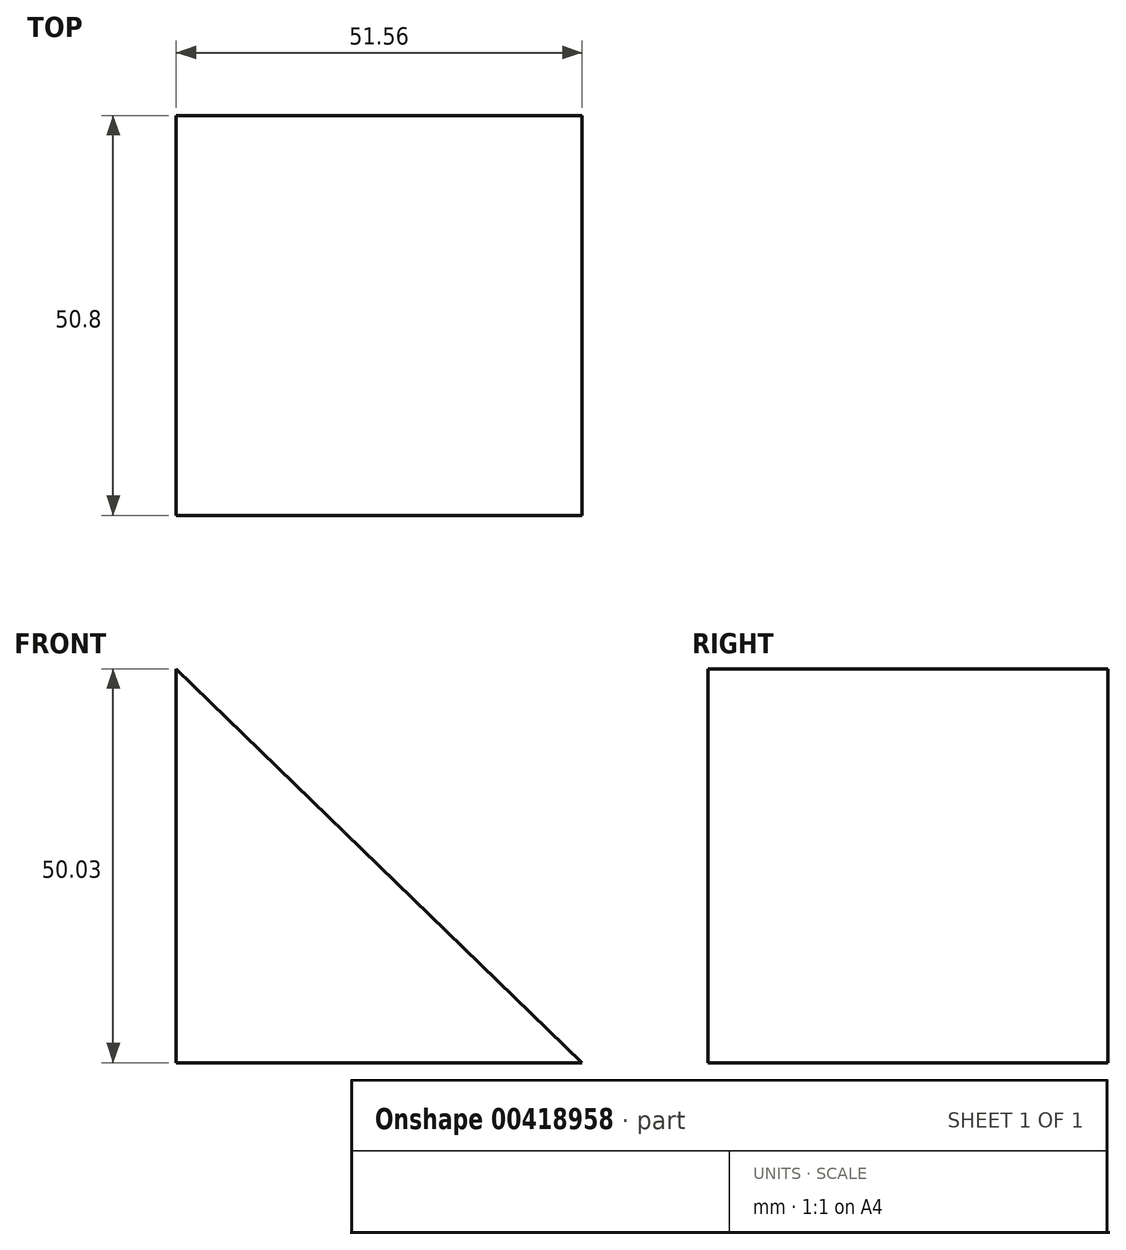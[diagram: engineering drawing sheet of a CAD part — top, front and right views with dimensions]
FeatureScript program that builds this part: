
annotation { "Feature Type Name" : "Feature", "Feature Type Description" : "" }
export const myFeature = defineFeature(function(context is Context, id is Id, definition is map)
    precondition{}
    {
        {
            var Q0;
            Q0=qCreatedBy(makeId("Front.planeOp"),FACE);
            var sketch = newSketch(context, id + "F0", { "sketchPlane" : qUnion([Q0])});
            skLineSegment(sketch, "E0", {"start": v(0, 0) * mm, "end": v(-51.56, 0) * mm});
            skLineSegment(sketch, "E1", {"start": v(-51.56, 50.03) * mm, "end": v(-51.56, 0) * mm});
            skLineSegment(sketch, "E2", {"start": v(-51.56, 50.03) * mm, "end": v(0, 0) * mm});
            skSolve(sketch);
        }
        {
            var Q0;
            Q0 = qSketchRegion(id + "F0", true);
            extrude(context, id + "F1", {"entities" : qUnion([Q0]), "depth" : 50.8 * mm});
        }
    });
